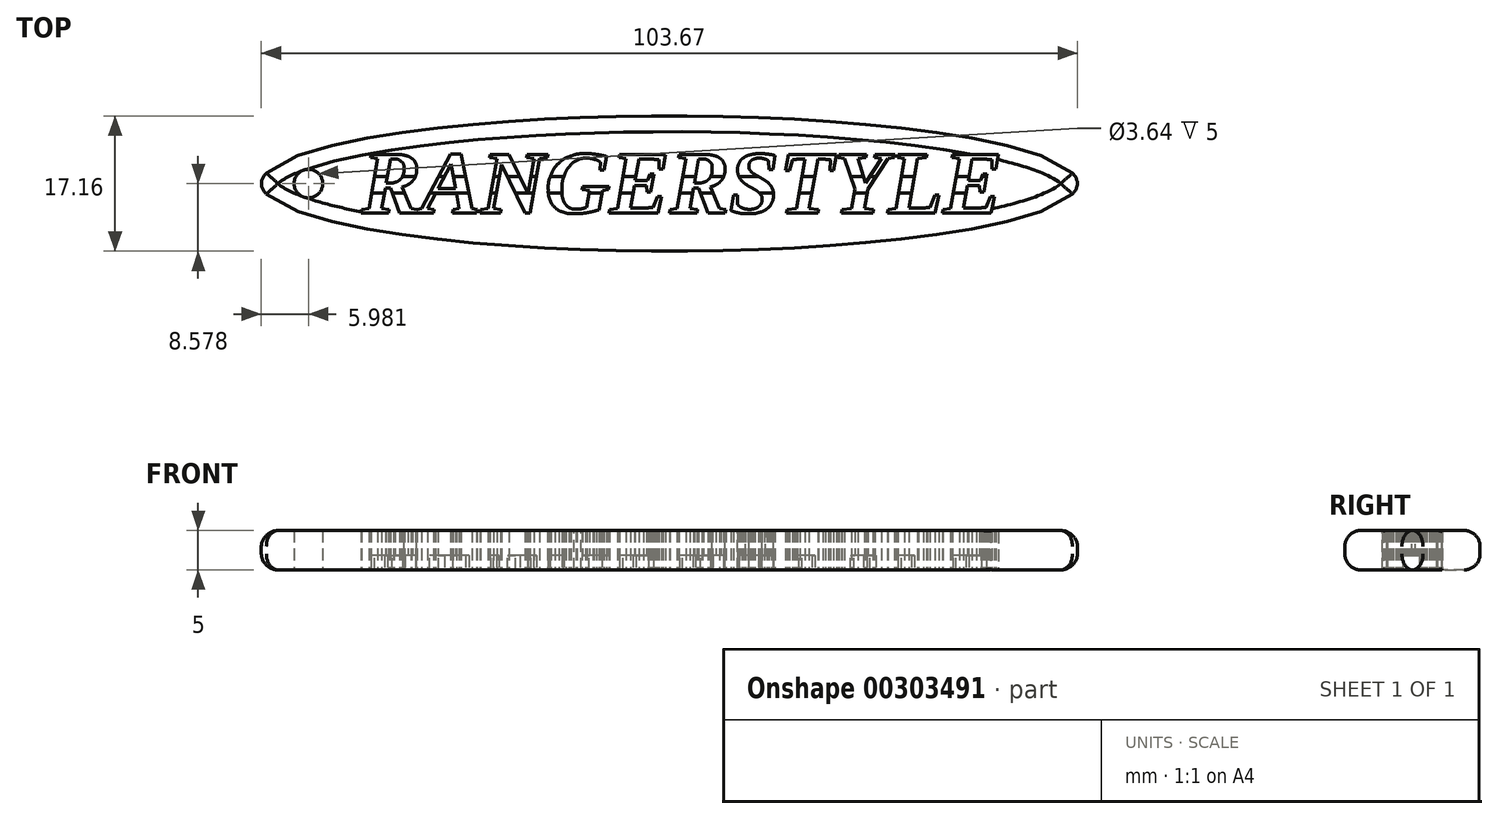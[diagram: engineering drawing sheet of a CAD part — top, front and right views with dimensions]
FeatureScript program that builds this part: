
annotation { "Feature Type Name" : "Feature", "Feature Type Description" : "" }
export const myFeature = defineFeature(function(context is Context, id is Id, definition is map)
    precondition{}
    {
        {
            var Q0;
            Q0=qCreatedBy(makeId("Top.planeOp"),FACE);
            var sketch = newSketch(context, id + "F0", { "sketchPlane" : qUnion([Q0])});
            skFitSpline(sketch, "E0", {"points": [v(-62.86, 19.24) * mm, v(-62.36, 19.24) * mm, v(-61.93, 19.2) * mm, v(-61.58, 19.12) * mm]});
            skFitSpline(sketch, "E1", {"points": [v(-61.58, 19.12) * mm, v(-61.22, 19.04) * mm, v(-60.92, 18.92) * mm, v(-60.7, 18.76) * mm]});
            skFitSpline(sketch, "E2", {"points": [v(-60.7, 18.76) * mm, v(-60.46, 18.6) * mm, v(-60.3, 18.42) * mm, v(-60.18, 18.18) * mm]});
            skFitSpline(sketch, "E3", {"points": [v(-60.18, 18.18) * mm, v(-60.07, 17.95) * mm, v(-60.01, 17.68) * mm, v(-60.01, 17.37) * mm]});
            skFitSpline(sketch, "E4", {"points": [v(-60.01, 17.37) * mm, v(-60.01, 17.05) * mm, v(-60.06, 16.76) * mm, v(-60.15, 16.5) * mm]});
            skFitSpline(sketch, "E5", {"points": [v(-60.15, 16.5) * mm, v(-60.24, 16.26) * mm, v(-60.37, 16.04) * mm, v(-60.53, 15.86) * mm]});
            skFitSpline(sketch, "E6", {"points": [v(-60.53, 15.86) * mm, v(-60.7, 15.68) * mm, v(-60.9, 15.53) * mm, v(-61.12, 15.4) * mm]});
            skFitSpline(sketch, "E7", {"points": [v(-61.12, 15.4) * mm, v(-61.34, 15.28) * mm, v(-61.58, 15.18) * mm, v(-61.84, 15.11) * mm]});
            skLineSegment(sketch, "E8", {"start": v(-63.99, 14.96) * mm, "end": v(-64.45, 12.36) * mm});
            skLineSegment(sketch, "E9", {"start": v(-64.45, 12.36) * mm, "end": v(-63.52, 12.21) * mm});
            skLineSegment(sketch, "E10", {"start": v(-63.52, 12.21) * mm, "end": v(-63.59, 11.8) * mm});
            skLineSegment(sketch, "E11", {"start": v(-63.59, 11.8) * mm, "end": v(-67.06, 11.8) * mm});
            skLineSegment(sketch, "E12", {"start": v(-67.06, 11.8) * mm, "end": v(-67, 12.21) * mm});
            skLineSegment(sketch, "E13", {"start": v(-67, 12.21) * mm, "end": v(-66.09, 12.36) * mm});
            skLineSegment(sketch, "E14", {"start": v(-66.09, 12.36) * mm, "end": v(-64.97, 18.7) * mm});
            skLineSegment(sketch, "E15", {"start": v(-64.97, 18.7) * mm, "end": v(-65.9, 18.84) * mm});
            skLineSegment(sketch, "E16", {"start": v(-65.9, 18.84) * mm, "end": v(-65.83, 19.24) * mm});
            skLineSegment(sketch, "E17", {"start": v(-65.83, 19.24) * mm, "end": v(-62.86, 19.24) * mm});
            skFitSpline(sketch, "E18", {"points": [v(-63.58, 15.57) * mm, v(-63.27, 15.57) * mm, v(-63, 15.6) * mm, v(-62.76, 15.68) * mm]});
            skFitSpline(sketch, "E19", {"points": [v(-62.76, 15.68) * mm, v(-62.52, 15.76) * mm, v(-62.32, 15.87) * mm, v(-62.15, 16.02) * mm]});
            skFitSpline(sketch, "E20", {"points": [v(-62.15, 16.02) * mm, v(-61.99, 16.16) * mm, v(-61.86, 16.34) * mm, v(-61.77, 16.55) * mm]});
            skFitSpline(sketch, "E21", {"points": [v(-61.77, 16.55) * mm, v(-61.68, 16.77) * mm, v(-61.64, 17) * mm, v(-61.64, 17.28) * mm]});
            skFitSpline(sketch, "E22", {"points": [v(-61.64, 17.28) * mm, v(-61.64, 17.76) * mm, v(-61.75, 18.1) * mm, v(-61.98, 18.32) * mm]});
            skFitSpline(sketch, "E23", {"points": [v(-61.98, 18.32) * mm, v(-62.2, 18.53) * mm, v(-62.52, 18.63) * mm, v(-62.96, 18.63) * mm]});
            skLineSegment(sketch, "E24", {"start": v(-61.84, 15.11) * mm, "end": v(-60.72, 12.36) * mm});
            skLineSegment(sketch, "E25", {"start": v(-60.72, 12.36) * mm, "end": v(-59.9, 12.21) * mm});
            skLineSegment(sketch, "E26", {"start": v(-59.9, 12.21) * mm, "end": v(-59.97, 11.8) * mm});
            skLineSegment(sketch, "E27", {"start": v(-60.05, 11.8) * mm, "end": v(-62.2, 11.8) * mm});
            skLineSegment(sketch, "E28", {"start": v(-62.2, 11.8) * mm, "end": v(-63.34, 14.96) * mm});
            skLineSegment(sketch, "E29", {"start": v(-63.34, 14.96) * mm, "end": v(-63.99, 14.96) * mm});
            skLineSegment(sketch, "E30", {"start": v(-62.96, 18.63) * mm, "end": v(-63.34, 18.63) * mm});
            skLineSegment(sketch, "E31", {"start": v(-63.34, 18.63) * mm, "end": v(-63.88, 15.57) * mm});
            skLineSegment(sketch, "E32", {"start": v(-63.88, 15.57) * mm, "end": v(-63.58, 15.57) * mm});
            skLineSegment(sketch, "E33", {"start": v(-57.8, 12.21) * mm, "end": v(-57.87, 11.8) * mm});
            skLineSegment(sketch, "E34", {"start": v(-57.87, 11.8) * mm, "end": v(-60.05, 11.8) * mm});
            skLineSegment(sketch, "E35", {"start": v(-60.05, 11.8) * mm, "end": v(-59.97, 12.21) * mm});
            skLineSegment(sketch, "E36", {"start": v(-59.97, 12.21) * mm, "end": v(-59.4, 12.36) * mm});
            skLineSegment(sketch, "E37", {"start": v(-59.4, 12.36) * mm, "end": v(-55.7, 19.3) * mm});
            skLineSegment(sketch, "E38", {"start": v(-55.7, 19.3) * mm, "end": v(-54.37, 19.3) * mm});
            skLineSegment(sketch, "E39", {"start": v(-54.37, 19.3) * mm, "end": v(-52.96, 12.36) * mm});
            skLineSegment(sketch, "E40", {"start": v(-52.96, 12.36) * mm, "end": v(-52.36, 12.21) * mm});
            skLineSegment(sketch, "E41", {"start": v(-52.36, 12.21) * mm, "end": v(-52.44, 11.8) * mm});
            skLineSegment(sketch, "E42", {"start": v(-52.44, 11.8) * mm, "end": v(-55.48, 11.8) * mm});
            skLineSegment(sketch, "E43", {"start": v(-55.48, 11.8) * mm, "end": v(-55.4, 12.21) * mm});
            skLineSegment(sketch, "E44", {"start": v(-55.4, 12.21) * mm, "end": v(-54.64, 12.36) * mm});
            skLineSegment(sketch, "E45", {"start": v(-54.64, 12.36) * mm, "end": v(-54.97, 14.29) * mm});
            skLineSegment(sketch, "E46", {"start": v(-54.97, 14.29) * mm, "end": v(-57.6, 14.29) * mm});
            skLineSegment(sketch, "E47", {"start": v(-57.6, 14.29) * mm, "end": v(-58.61, 12.36) * mm});
            skLineSegment(sketch, "E48", {"start": v(-58.61, 12.36) * mm, "end": v(-57.8, 12.21) * mm});
            skLineSegment(sketch, "E49", {"start": v(-55.65, 18) * mm, "end": v(-57.28, 14.9) * mm});
            skLineSegment(sketch, "E50", {"start": v(-57.28, 14.9) * mm, "end": v(-55.09, 14.9) * mm});
            skLineSegment(sketch, "E51", {"start": v(-55.09, 14.9) * mm, "end": v(-55.65, 18) * mm});
            skFitSpline(sketch, "E52", {"points": [v(-43.3, 14.7) * mm, v(-43.3, 15.45) * mm, v(-43.17, 16.1) * mm, v(-42.93, 16.68) * mm]});
            skFitSpline(sketch, "E53", {"points": [v(-42.93, 16.68) * mm, v(-42.69, 17.25) * mm, v(-42.35, 17.74) * mm, v(-41.93, 18.13) * mm]});
            skFitSpline(sketch, "E54", {"points": [v(-41.93, 18.13) * mm, v(-41.5, 18.52) * mm, v(-41, 18.82) * mm, v(-40.42, 19.02) * mm]});
            skFitSpline(sketch, "E55", {"points": [v(-40.42, 19.02) * mm, v(-39.85, 19.22) * mm, v(-39.23, 19.32) * mm, v(-38.56, 19.32) * mm]});
            skFitSpline(sketch, "E56", {"points": [v(-38.56, 19.32) * mm, v(-38.05, 19.32) * mm, v(-37.58, 19.3) * mm, v(-37.15, 19.23) * mm]});
            skFitSpline(sketch, "E57", {"points": [v(-37.15, 19.23) * mm, v(-36.73, 19.17) * mm, v(-36.32, 19.09) * mm, v(-35.92, 18.98) * mm]});
            skLineSegment(sketch, "E58", {"start": v(-45.1, 18.7) * mm, "end": v(-46.06, 18.84) * mm});
            skLineSegment(sketch, "E59", {"start": v(-46.06, 18.84) * mm, "end": v(-45.99, 19.24) * mm});
            skLineSegment(sketch, "E60", {"start": v(-45.99, 19.24) * mm, "end": v(-43.35, 19.24) * mm});
            skLineSegment(sketch, "E61", {"start": v(-43.35, 19.24) * mm, "end": v(-43.42, 18.84) * mm});
            skLineSegment(sketch, "E62", {"start": v(-43.42, 18.84) * mm, "end": v(-44.4, 18.7) * mm});
            skLineSegment(sketch, "E63", {"start": v(-44.4, 18.7) * mm, "end": v(-45.6, 11.8) * mm});
            skLineSegment(sketch, "E64", {"start": v(-45.6, 11.8) * mm, "end": v(-46.24, 11.8) * mm});
            skLineSegment(sketch, "E65", {"start": v(-46.24, 11.8) * mm, "end": v(-49.24, 17.97) * mm});
            skLineSegment(sketch, "E66", {"start": v(-49.24, 17.97) * mm, "end": v(-50.25, 12.36) * mm});
            skLineSegment(sketch, "E67", {"start": v(-50.25, 12.36) * mm, "end": v(-49.28, 12.21) * mm});
            skLineSegment(sketch, "E68", {"start": v(-49.28, 12.21) * mm, "end": v(-49.34, 11.8) * mm});
            skLineSegment(sketch, "E69", {"start": v(-49.34, 11.8) * mm, "end": v(-51.99, 11.8) * mm});
            skLineSegment(sketch, "E70", {"start": v(-51.99, 11.8) * mm, "end": v(-51.92, 12.21) * mm});
            skLineSegment(sketch, "E71", {"start": v(-51.92, 12.21) * mm, "end": v(-50.94, 12.36) * mm});
            skLineSegment(sketch, "E72", {"start": v(-50.94, 12.36) * mm, "end": v(-49.83, 18.7) * mm});
            skLineSegment(sketch, "E73", {"start": v(-49.83, 18.7) * mm, "end": v(-50.75, 18.84) * mm});
            skLineSegment(sketch, "E74", {"start": v(-50.75, 18.84) * mm, "end": v(-50.68, 19.24) * mm});
            skLineSegment(sketch, "E75", {"start": v(-50.68, 19.24) * mm, "end": v(-48.28, 19.24) * mm});
            skLineSegment(sketch, "E76", {"start": v(-48.28, 19.24) * mm, "end": v(-45.87, 14.29) * mm});
            skLineSegment(sketch, "E77", {"start": v(-45.87, 14.29) * mm, "end": v(-45.1, 18.7) * mm});
            skFitSpline(sketch, "E78", {"points": [v(-36.69, 18.24) * mm, v(-36.9, 18.4) * mm, v(-37.16, 18.52) * mm, v(-37.46, 18.6) * mm]});
            skFitSpline(sketch, "E79", {"points": [v(-37.46, 18.6) * mm, v(-37.75, 18.7) * mm, v(-38.09, 18.74) * mm, v(-38.46, 18.74) * mm]});
            skFitSpline(sketch, "E80", {"points": [v(-38.46, 18.74) * mm, v(-38.88, 18.74) * mm, v(-39.27, 18.65) * mm, v(-39.65, 18.47) * mm]});
            skFitSpline(sketch, "E81", {"points": [v(-39.65, 18.47) * mm, v(-40.02, 18.29) * mm, v(-40.35, 18.02) * mm, v(-40.64, 17.67) * mm]});
            skFitSpline(sketch, "E82", {"points": [v(-40.64, 17.67) * mm, v(-40.92, 17.33) * mm, v(-41.15, 16.9) * mm, v(-41.32, 16.38) * mm]});
            skFitSpline(sketch, "E83", {"points": [v(-41.32, 16.38) * mm, v(-41.48, 15.86) * mm, v(-41.57, 15.26) * mm, v(-41.57, 14.6) * mm]});
            skFitSpline(sketch, "E84", {"points": [v(-41.57, 14.6) * mm, v(-41.57, 14.2) * mm, v(-41.52, 13.87) * mm, v(-41.43, 13.58) * mm]});
            skFitSpline(sketch, "E85", {"points": [v(-41.43, 13.58) * mm, v(-41.34, 13.28) * mm, v(-41.22, 13.04) * mm, v(-41.06, 12.84) * mm]});
            skFitSpline(sketch, "E86", {"points": [v(-41.06, 12.84) * mm, v(-40.9, 12.65) * mm, v(-40.71, 12.5) * mm, v(-40.5, 12.41) * mm]});
            skFitSpline(sketch, "E87", {"points": [v(-40.5, 12.41) * mm, v(-40.27, 12.32) * mm, v(-40.02, 12.27) * mm, v(-39.75, 12.27) * mm]});
            skFitSpline(sketch, "E88", {"points": [v(-39.75, 12.27) * mm, v(-39.47, 12.27) * mm, v(-39.21, 12.3) * mm, v(-38.98, 12.35) * mm]});
            skFitSpline(sketch, "E89", {"points": [v(-38.98, 12.35) * mm, v(-38.75, 12.4) * mm, v(-38.57, 12.45) * mm, v(-38.44, 12.5) * mm]});
            skLineSegment(sketch, "E90", {"start": v(-35.92, 18.98) * mm, "end": v(-36.23, 17.27) * mm});
            skLineSegment(sketch, "E91", {"start": v(-36.23, 17.27) * mm, "end": v(-36.7, 17.27) * mm});
            skLineSegment(sketch, "E92", {"start": v(-36.7, 17.27) * mm, "end": v(-36.69, 18.24) * mm});
            skFitSpline(sketch, "E93", {"points": [v(-36.85, 12.2) * mm, v(-37.1, 12.12) * mm, v(-37.35, 12.05) * mm, v(-37.6, 11.99) * mm]});
            skFitSpline(sketch, "E94", {"points": [v(-37.6, 11.99) * mm, v(-37.84, 11.93) * mm, v(-38.09, 11.87) * mm, v(-38.35, 11.83) * mm]});
            skFitSpline(sketch, "E95", {"points": [v(-38.35, 11.83) * mm, v(-38.6, 11.79) * mm, v(-38.87, 11.75) * mm, v(-39.14, 11.73) * mm]});
            skFitSpline(sketch, "E96", {"points": [v(-39.14, 11.73) * mm, v(-39.42, 11.7) * mm, v(-39.7, 11.7) * mm, v(-40, 11.7) * mm]});
            skFitSpline(sketch, "E97", {"points": [v(-40, 11.7) * mm, v(-40.53, 11.7) * mm, v(-41, 11.77) * mm, v(-41.41, 11.9) * mm]});
            skFitSpline(sketch, "E98", {"points": [v(-41.41, 11.9) * mm, v(-41.82, 12.04) * mm, v(-42.16, 12.24) * mm, v(-42.44, 12.5) * mm]});
            skFitSpline(sketch, "E99", {"points": [v(-42.44, 12.5) * mm, v(-42.72, 12.76) * mm, v(-42.93, 13.08) * mm, v(-43.07, 13.45) * mm]});
            skFitSpline(sketch, "E100", {"points": [v(-43.07, 13.45) * mm, v(-43.22, 13.82) * mm, v(-43.3, 14.24) * mm, v(-43.3, 14.7) * mm]});
            skLineSegment(sketch, "E101", {"start": v(-38.44, 12.5) * mm, "end": v(-38.06, 14.61) * mm});
            skLineSegment(sketch, "E102", {"start": v(-38.06, 14.61) * mm, "end": v(-38.99, 14.8) * mm});
            skLineSegment(sketch, "E103", {"start": v(-38.99, 14.8) * mm, "end": v(-38.92, 15.17) * mm});
            skLineSegment(sketch, "E104", {"start": v(-38.92, 15.17) * mm, "end": v(-35.6, 15.17) * mm});
            skLineSegment(sketch, "E105", {"start": v(-35.6, 15.17) * mm, "end": v(-35.67, 14.8) * mm});
            skLineSegment(sketch, "E106", {"start": v(-35.67, 14.8) * mm, "end": v(-36.43, 14.61) * mm});
            skLineSegment(sketch, "E107", {"start": v(-36.43, 14.61) * mm, "end": v(-36.85, 12.2) * mm});
            skFitSpline(sketch, "E108", {"points": [v(-29.22, 18.55) * mm, v(-29.34, 18.57) * mm, v(-29.47, 18.58) * mm, v(-29.63, 18.6) * mm]});
            skFitSpline(sketch, "E109", {"points": [v(-29.63, 18.6) * mm, v(-29.78, 18.6) * mm, v(-29.94, 18.61) * mm, v(-30.1, 18.61) * mm]});
            skFitSpline(sketch, "E110", {"points": [v(-30.1, 18.61) * mm, v(-30.27, 18.62) * mm, v(-30.43, 18.63) * mm, v(-30.59, 18.63) * mm]});
            skFitSpline(sketch, "E111", {"points": [v(-30.59, 18.63) * mm, v(-30.74, 18.63) * mm, v(-30.88, 18.63) * mm, v(-31, 18.63) * mm]});
            skLineSegment(sketch, "E112", {"start": v(-35.5, 12.21) * mm, "end": v(-34.51, 12.36) * mm});
            skLineSegment(sketch, "E113", {"start": v(-34.51, 12.36) * mm, "end": v(-33.4, 18.7) * mm});
            skLineSegment(sketch, "E114", {"start": v(-33.4, 18.7) * mm, "end": v(-34.32, 18.84) * mm});
            skLineSegment(sketch, "E115", {"start": v(-34.32, 18.84) * mm, "end": v(-34.25, 19.24) * mm});
            skLineSegment(sketch, "E116", {"start": v(-34.25, 19.24) * mm, "end": v(-28.42, 19.24) * mm});
            skLineSegment(sketch, "E117", {"start": v(-28.42, 19.24) * mm, "end": v(-28.75, 17.35) * mm});
            skLineSegment(sketch, "E118", {"start": v(-28.75, 17.35) * mm, "end": v(-29.26, 17.35) * mm});
            skLineSegment(sketch, "E119", {"start": v(-29.26, 17.35) * mm, "end": v(-29.22, 18.55) * mm});
            skFitSpline(sketch, "E120", {"points": [v(-31.85, 12.42) * mm, v(-31.62, 12.42) * mm, v(-31.4, 12.42) * mm, v(-31.2, 12.42) * mm]});
            skFitSpline(sketch, "E121", {"points": [v(-31.2, 12.42) * mm, v(-31, 12.43) * mm, v(-30.82, 12.44) * mm, v(-30.66, 12.45) * mm]});
            skFitSpline(sketch, "E122", {"points": [v(-30.66, 12.45) * mm, v(-30.5, 12.45) * mm, v(-30.36, 12.46) * mm, v(-30.24, 12.47) * mm]});
            skFitSpline(sketch, "E123", {"points": [v(-30.24, 12.47) * mm, v(-30.12, 12.48) * mm, v(-30.04, 12.5) * mm, v(-29.98, 12.5) * mm]});
            skLineSegment(sketch, "E124", {"start": v(-31, 18.63) * mm, "end": v(-31.77, 18.63) * mm});
            skLineSegment(sketch, "E125", {"start": v(-31.77, 18.63) * mm, "end": v(-32.25, 15.9) * mm});
            skLineSegment(sketch, "E126", {"start": v(-32.25, 15.9) * mm, "end": v(-30.7, 15.9) * mm});
            skLineSegment(sketch, "E127", {"start": v(-30.7, 15.9) * mm, "end": v(-30.38, 16.72) * mm});
            skLineSegment(sketch, "E128", {"start": v(-30.38, 16.72) * mm, "end": v(-29.88, 16.72) * mm});
            skLineSegment(sketch, "E129", {"start": v(-29.88, 16.72) * mm, "end": v(-30.29, 14.44) * mm});
            skLineSegment(sketch, "E130", {"start": v(-30.29, 14.44) * mm, "end": v(-30.78, 14.44) * mm});
            skLineSegment(sketch, "E131", {"start": v(-30.78, 14.44) * mm, "end": v(-30.8, 15.28) * mm});
            skLineSegment(sketch, "E132", {"start": v(-30.8, 15.28) * mm, "end": v(-32.36, 15.28) * mm});
            skLineSegment(sketch, "E133", {"start": v(-32.36, 15.28) * mm, "end": v(-32.86, 12.42) * mm});
            skLineSegment(sketch, "E134", {"start": v(-32.86, 12.42) * mm, "end": v(-31.85, 12.42) * mm});
            skLineSegment(sketch, "E135", {"start": v(-29.98, 12.5) * mm, "end": v(-29.4, 13.88) * mm});
            skLineSegment(sketch, "E136", {"start": v(-29.4, 13.88) * mm, "end": v(-28.9, 13.88) * mm});
            skLineSegment(sketch, "E137", {"start": v(-28.9, 13.88) * mm, "end": v(-29.37, 11.8) * mm});
            skLineSegment(sketch, "E138", {"start": v(-29.37, 11.8) * mm, "end": v(-35.56, 11.8) * mm});
            skLineSegment(sketch, "E139", {"start": v(-35.56, 11.8) * mm, "end": v(-35.5, 12.21) * mm});
            skLineSegment(sketch, "E140", {"start": v(-35.5, 12.21) * mm, "end": v(-35.5, 12.21) * mm});
            skLineSegment(sketch, "E141", {"start": v(-31.63, 12.42) * mm, "end": v(-29.98, 12.5) * mm});
            skFitSpline(sketch, "E142", {"points": [v(-23.7, 19.24) * mm, v(-23.2, 19.24) * mm, v(-22.78, 19.2) * mm, v(-22.42, 19.12) * mm]});
            skFitSpline(sketch, "E143", {"points": [v(-22.42, 19.12) * mm, v(-22.06, 19.04) * mm, v(-21.77, 18.92) * mm, v(-21.54, 18.76) * mm]});
            skFitSpline(sketch, "E144", {"points": [v(-21.54, 18.76) * mm, v(-21.3, 18.6) * mm, v(-21.14, 18.42) * mm, v(-21.02, 18.18) * mm]});
            skFitSpline(sketch, "E145", {"points": [v(-21.02, 18.18) * mm, v(-20.91, 17.95) * mm, v(-20.86, 17.68) * mm, v(-20.86, 17.37) * mm]});
            skFitSpline(sketch, "E146", {"points": [v(-20.86, 17.37) * mm, v(-20.86, 17.05) * mm, v(-20.9, 16.76) * mm, v(-21, 16.5) * mm]});
            skFitSpline(sketch, "E147", {"points": [v(-21, 16.5) * mm, v(-21.09, 16.26) * mm, v(-21.22, 16.04) * mm, v(-21.38, 15.86) * mm]});
            skFitSpline(sketch, "E148", {"points": [v(-21.38, 15.86) * mm, v(-21.54, 15.68) * mm, v(-21.74, 15.53) * mm, v(-21.96, 15.4) * mm]});
            skFitSpline(sketch, "E149", {"points": [v(-21.96, 15.4) * mm, v(-22.18, 15.28) * mm, v(-22.42, 15.18) * mm, v(-22.68, 15.11) * mm]});
            skLineSegment(sketch, "E150", {"start": v(-24.83, 14.96) * mm, "end": v(-25.3, 12.36) * mm});
            skLineSegment(sketch, "E151", {"start": v(-25.3, 12.36) * mm, "end": v(-24.37, 12.21) * mm});
            skLineSegment(sketch, "E152", {"start": v(-24.37, 12.21) * mm, "end": v(-24.43, 11.8) * mm});
            skLineSegment(sketch, "E153", {"start": v(-24.43, 11.8) * mm, "end": v(-27.9, 11.8) * mm});
            skLineSegment(sketch, "E154", {"start": v(-27.9, 11.8) * mm, "end": v(-27.84, 12.21) * mm});
            skLineSegment(sketch, "E155", {"start": v(-27.84, 12.21) * mm, "end": v(-26.93, 12.36) * mm});
            skLineSegment(sketch, "E156", {"start": v(-26.93, 12.36) * mm, "end": v(-25.82, 18.7) * mm});
            skLineSegment(sketch, "E157", {"start": v(-25.82, 18.7) * mm, "end": v(-26.74, 18.84) * mm});
            skLineSegment(sketch, "E158", {"start": v(-26.74, 18.84) * mm, "end": v(-26.67, 19.24) * mm});
            skLineSegment(sketch, "E159", {"start": v(-26.67, 19.24) * mm, "end": v(-23.7, 19.24) * mm});
            skFitSpline(sketch, "E160", {"points": [v(-24.42, 15.57) * mm, v(-24.12, 15.57) * mm, v(-23.85, 15.6) * mm, v(-23.6, 15.68) * mm]});
            skFitSpline(sketch, "E161", {"points": [v(-23.6, 15.68) * mm, v(-23.37, 15.76) * mm, v(-23.16, 15.87) * mm, v(-23, 16.02) * mm]});
            skFitSpline(sketch, "E162", {"points": [v(-23, 16.02) * mm, v(-22.83, 16.16) * mm, v(-22.7, 16.34) * mm, v(-22.62, 16.55) * mm]});
            skFitSpline(sketch, "E163", {"points": [v(-22.62, 16.55) * mm, v(-22.53, 16.77) * mm, v(-22.48, 17) * mm, v(-22.48, 17.28) * mm]});
            skFitSpline(sketch, "E164", {"points": [v(-22.48, 17.28) * mm, v(-22.48, 17.76) * mm, v(-22.6, 18.1) * mm, v(-22.82, 18.32) * mm]});
            skFitSpline(sketch, "E165", {"points": [v(-22.82, 18.32) * mm, v(-23.04, 18.53) * mm, v(-23.37, 18.63) * mm, v(-23.8, 18.63) * mm]});
            skLineSegment(sketch, "E166", {"start": v(-22.68, 15.11) * mm, "end": v(-21.57, 12.36) * mm});
            skLineSegment(sketch, "E167", {"start": v(-21.57, 12.36) * mm, "end": v(-20.75, 12.21) * mm});
            skLineSegment(sketch, "E168", {"start": v(-20.75, 12.21) * mm, "end": v(-20.82, 11.8) * mm});
            skLineSegment(sketch, "E169", {"start": v(-20.82, 11.8) * mm, "end": v(-23.04, 11.8) * mm});
            skLineSegment(sketch, "E170", {"start": v(-23.04, 11.8) * mm, "end": v(-24.19, 14.96) * mm});
            skLineSegment(sketch, "E171", {"start": v(-24.19, 14.96) * mm, "end": v(-24.83, 14.96) * mm});
            skFitSpline(sketch, "E172", {"points": [v(-17.92, 11.7) * mm, v(-18.4, 11.7) * mm, v(-18.83, 11.74) * mm, v(-19.2, 11.82) * mm]});
            skFitSpline(sketch, "E173", {"points": [v(-19.2, 11.82) * mm, v(-19.56, 11.9) * mm, v(-19.86, 12) * mm, v(-20.1, 12.1) * mm]});
            skLineSegment(sketch, "E174", {"start": v(-23.8, 18.63) * mm, "end": v(-24.18, 18.63) * mm});
            skLineSegment(sketch, "E175", {"start": v(-24.18, 18.63) * mm, "end": v(-24.73, 15.57) * mm});
            skLineSegment(sketch, "E176", {"start": v(-24.73, 15.57) * mm, "end": v(-24.42, 15.57) * mm});
            skFitSpline(sketch, "E177", {"points": [v(-19.26, 12.9) * mm, v(-19.2, 12.8) * mm, v(-19.11, 12.72) * mm, v(-19.01, 12.64) * mm]});
            skFitSpline(sketch, "E178", {"points": [v(-19.01, 12.64) * mm, v(-18.9, 12.56) * mm, v(-18.8, 12.5) * mm, v(-18.67, 12.43) * mm]});
            skFitSpline(sketch, "E179", {"points": [v(-18.67, 12.43) * mm, v(-18.54, 12.38) * mm, v(-18.4, 12.33) * mm, v(-18.26, 12.3) * mm]});
            skFitSpline(sketch, "E180", {"points": [v(-18.26, 12.3) * mm, v(-18.12, 12.27) * mm, v(-17.97, 12.26) * mm, v(-17.82, 12.26) * mm]});
            skFitSpline(sketch, "E181", {"points": [v(-17.82, 12.26) * mm, v(-17.53, 12.26) * mm, v(-17.28, 12.29) * mm, v(-17.07, 12.35) * mm]});
            skFitSpline(sketch, "E182", {"points": [v(-17.07, 12.35) * mm, v(-16.85, 12.42) * mm, v(-16.68, 12.5) * mm, v(-16.54, 12.62) * mm]});
            skFitSpline(sketch, "E183", {"points": [v(-16.54, 12.62) * mm, v(-16.4, 12.74) * mm, v(-16.3, 12.87) * mm, v(-16.24, 13.03) * mm]});
            skFitSpline(sketch, "E184", {"points": [v(-16.24, 13.03) * mm, v(-16.17, 13.18) * mm, v(-16.14, 13.35) * mm, v(-16.14, 13.53) * mm]});
            skFitSpline(sketch, "E185", {"points": [v(-16.14, 13.53) * mm, v(-16.14, 13.73) * mm, v(-16.18, 13.9) * mm, v(-16.27, 14.05) * mm]});
            skFitSpline(sketch, "E186", {"points": [v(-16.27, 14.05) * mm, v(-16.36, 14.2) * mm, v(-16.48, 14.33) * mm, v(-16.62, 14.45) * mm]});
            skFitSpline(sketch, "E187", {"points": [v(-16.62, 14.45) * mm, v(-16.77, 14.57) * mm, v(-16.93, 14.69) * mm, v(-17.12, 14.8) * mm]});
            skFitSpline(sketch, "E188", {"points": [v(-17.12, 14.8) * mm, v(-17.3, 14.9) * mm, v(-17.5, 15) * mm, v(-17.69, 15.11) * mm]});
            skFitSpline(sketch, "E189", {"points": [v(-17.69, 15.11) * mm, v(-17.88, 15.22) * mm, v(-18.07, 15.34) * mm, v(-18.25, 15.47) * mm]});
            skFitSpline(sketch, "E190", {"points": [v(-18.25, 15.47) * mm, v(-18.44, 15.6) * mm, v(-18.6, 15.74) * mm, v(-18.75, 15.9) * mm]});
            skFitSpline(sketch, "E191", {"points": [v(-18.75, 15.9) * mm, v(-18.9, 16.08) * mm, v(-19.01, 16.27) * mm, v(-19.1, 16.48) * mm]});
            skFitSpline(sketch, "E192", {"points": [v(-19.1, 16.48) * mm, v(-19.19, 16.7) * mm, v(-19.23, 16.95) * mm, v(-19.23, 17.23) * mm]});
            skFitSpline(sketch, "E193", {"points": [v(-19.23, 17.23) * mm, v(-19.23, 17.59) * mm, v(-19.17, 17.9) * mm, v(-19.04, 18.15) * mm]});
            skFitSpline(sketch, "E194", {"points": [v(-19.04, 18.15) * mm, v(-18.9, 18.42) * mm, v(-18.72, 18.63) * mm, v(-18.47, 18.8) * mm]});
            skFitSpline(sketch, "E195", {"points": [v(-18.47, 18.8) * mm, v(-18.22, 18.98) * mm, v(-17.91, 19.11) * mm, v(-17.55, 19.2) * mm]});
            skFitSpline(sketch, "E196", {"points": [v(-17.55, 19.2) * mm, v(-17.2, 19.28) * mm, v(-16.79, 19.32) * mm, v(-16.34, 19.32) * mm]});
            skFitSpline(sketch, "E197", {"points": [v(-16.34, 19.32) * mm, v(-16.02, 19.32) * mm, v(-15.7, 19.3) * mm, v(-15.37, 19.26) * mm]});
            skFitSpline(sketch, "E198", {"points": [v(-15.37, 19.26) * mm, v(-15.04, 19.21) * mm, v(-14.74, 19.16) * mm, v(-14.47, 19.09) * mm]});
            skLineSegment(sketch, "E199", {"start": v(-20.1, 12.1) * mm, "end": v(-19.75, 14.09) * mm});
            skLineSegment(sketch, "E200", {"start": v(-19.75, 14.09) * mm, "end": v(-19.26, 14.09) * mm});
            skLineSegment(sketch, "E201", {"start": v(-19.26, 14.09) * mm, "end": v(-19.26, 12.9) * mm});
            skFitSpline(sketch, "E202", {"points": [v(-15.32, 18.4) * mm, v(-15.46, 18.51) * mm, v(-15.63, 18.6) * mm, v(-15.83, 18.65) * mm]});
            skFitSpline(sketch, "E203", {"points": [v(-15.83, 18.65) * mm, v(-16.02, 18.72) * mm, v(-16.24, 18.75) * mm, v(-16.49, 18.75) * mm]});
            skFitSpline(sketch, "E204", {"points": [v(-16.49, 18.75) * mm, v(-16.72, 18.75) * mm, v(-16.92, 18.72) * mm, v(-17.1, 18.66) * mm]});
            skFitSpline(sketch, "E205", {"points": [v(-17.1, 18.66) * mm, v(-17.26, 18.6) * mm, v(-17.4, 18.54) * mm, v(-17.51, 18.44) * mm]});
            skFitSpline(sketch, "E206", {"points": [v(-17.51, 18.44) * mm, v(-17.62, 18.35) * mm, v(-17.7, 18.24) * mm, v(-17.75, 18.12) * mm]});
            skFitSpline(sketch, "E207", {"points": [v(-17.75, 18.12) * mm, v(-17.8, 18) * mm, v(-17.83, 17.87) * mm, v(-17.83, 17.73) * mm]});
            skFitSpline(sketch, "E208", {"points": [v(-17.83, 17.73) * mm, v(-17.83, 17.56) * mm, v(-17.78, 17.4) * mm, v(-17.7, 17.26) * mm]});
            skFitSpline(sketch, "E209", {"points": [v(-17.7, 17.26) * mm, v(-17.6, 17.13) * mm, v(-17.49, 17) * mm, v(-17.34, 16.89) * mm]});
            skFitSpline(sketch, "E210", {"points": [v(-17.34, 16.89) * mm, v(-17.2, 16.77) * mm, v(-17.02, 16.66) * mm, v(-16.84, 16.56) * mm]});
            skFitSpline(sketch, "E211", {"points": [v(-16.84, 16.56) * mm, v(-16.65, 16.45) * mm, v(-16.46, 16.35) * mm, v(-16.27, 16.24) * mm]});
            skFitSpline(sketch, "E212", {"points": [v(-16.27, 16.24) * mm, v(-16.07, 16.13) * mm, v(-15.88, 16) * mm, v(-15.7, 15.88) * mm]});
            skFitSpline(sketch, "E213", {"points": [v(-15.7, 15.88) * mm, v(-15.5, 15.75) * mm, v(-15.34, 15.6) * mm, v(-15.2, 15.44) * mm]});
            skFitSpline(sketch, "E214", {"points": [v(-15.2, 15.44) * mm, v(-15.05, 15.28) * mm, v(-14.93, 15.09) * mm, v(-14.84, 14.88) * mm]});
            skFitSpline(sketch, "E215", {"points": [v(-14.84, 14.88) * mm, v(-14.75, 14.67) * mm, v(-14.7, 14.43) * mm, v(-14.7, 14.15) * mm]});
            skFitSpline(sketch, "E216", {"points": [v(-14.7, 14.15) * mm, v(-14.7, 13.75) * mm, v(-14.78, 13.39) * mm, v(-14.92, 13.08) * mm]});
            skFitSpline(sketch, "E217", {"points": [v(-14.92, 13.08) * mm, v(-15.06, 12.78) * mm, v(-15.27, 12.52) * mm, v(-15.54, 12.31) * mm]});
            skFitSpline(sketch, "E218", {"points": [v(-15.54, 12.31) * mm, v(-15.82, 12.1) * mm, v(-16.15, 11.96) * mm, v(-16.55, 11.85) * mm]});
            skFitSpline(sketch, "E219", {"points": [v(-16.55, 11.85) * mm, v(-16.95, 11.75) * mm, v(-17.4, 11.7) * mm, v(-17.92, 11.7) * mm]});
            skLineSegment(sketch, "E220", {"start": v(-14.47, 19.09) * mm, "end": v(-14.78, 17.32) * mm});
            skLineSegment(sketch, "E221", {"start": v(-14.78, 17.32) * mm, "end": v(-15.28, 17.32) * mm});
            skLineSegment(sketch, "E222", {"start": v(-15.28, 17.32) * mm, "end": v(-15.32, 18.4) * mm});
            skFitSpline(sketch, "E223", {"points": [v(-11.02, 18.65) * mm, v(-11.1, 18.65) * mm, v(-11.2, 18.65) * mm, v(-11.32, 18.64) * mm]});
            skFitSpline(sketch, "E224", {"points": [v(-11.32, 18.64) * mm, v(-11.43, 18.64) * mm, v(-11.55, 18.63) * mm, v(-11.67, 18.62) * mm]});
            skFitSpline(sketch, "E225", {"points": [v(-11.67, 18.62) * mm, v(-11.78, 18.6) * mm, v(-11.9, 18.6) * mm, v(-12, 18.58) * mm]});
            skFitSpline(sketch, "E226", {"points": [v(-12, 18.58) * mm, v(-12.1, 18.57) * mm, v(-12.2, 18.56) * mm, v(-12.27, 18.54) * mm]});
            skLineSegment(sketch, "E227", {"start": v(-13.07, 11.8) * mm, "end": v(-13, 12.21) * mm});
            skLineSegment(sketch, "E228", {"start": v(-13, 12.21) * mm, "end": v(-11.8, 12.36) * mm});
            skLineSegment(sketch, "E229", {"start": v(-11.8, 12.36) * mm, "end": v(-10.68, 18.65) * mm});
            skLineSegment(sketch, "E230", {"start": v(-10.68, 18.65) * mm, "end": v(-11.02, 18.65) * mm});
            skFitSpline(sketch, "E231", {"points": [v(-7.47, 18.54) * mm, v(-7.53, 18.56) * mm, v(-7.62, 18.57) * mm, v(-7.73, 18.58) * mm]});
            skFitSpline(sketch, "E232", {"points": [v(-7.73, 18.58) * mm, v(-7.83, 18.6) * mm, v(-7.94, 18.6) * mm, v(-8.06, 18.6) * mm]});
            skFitSpline(sketch, "E233", {"points": [v(-8.06, 18.6) * mm, v(-8.18, 18.62) * mm, v(-8.3, 18.63) * mm, v(-8.41, 18.63) * mm]});
            skFitSpline(sketch, "E234", {"points": [v(-8.41, 18.63) * mm, v(-8.53, 18.64) * mm, v(-8.63, 18.64) * mm, v(-8.71, 18.64) * mm]});
            skLineSegment(sketch, "E235", {"start": v(-12.27, 18.54) * mm, "end": v(-12.68, 17.16) * mm});
            skLineSegment(sketch, "E236", {"start": v(-12.68, 17.16) * mm, "end": v(-13.16, 17.16) * mm});
            skLineSegment(sketch, "E237", {"start": v(-13.16, 17.16) * mm, "end": v(-12.8, 19.24) * mm});
            skLineSegment(sketch, "E238", {"start": v(-12.8, 19.24) * mm, "end": v(-6.69, 19.24) * mm});
            skLineSegment(sketch, "E239", {"start": v(-6.69, 19.24) * mm, "end": v(-7.05, 17.16) * mm});
            skLineSegment(sketch, "E240", {"start": v(-7.05, 17.16) * mm, "end": v(-7.54, 17.16) * mm});
            skLineSegment(sketch, "E241", {"start": v(-7.54, 17.16) * mm, "end": v(-7.47, 18.54) * mm});
            skLineSegment(sketch, "E242", {"start": v(-8.71, 18.64) * mm, "end": v(-9.04, 18.64) * mm});
            skLineSegment(sketch, "E243", {"start": v(-9.04, 18.64) * mm, "end": v(-10.15, 12.36) * mm});
            skLineSegment(sketch, "E244", {"start": v(-10.15, 12.36) * mm, "end": v(-9, 12.21) * mm});
            skLineSegment(sketch, "E245", {"start": v(-9, 12.21) * mm, "end": v(-9.06, 11.8) * mm});
            skLineSegment(sketch, "E246", {"start": v(-9.06, 11.8) * mm, "end": v(-13.07, 11.8) * mm});
            skLineSegment(sketch, "E247", {"start": v(-2.72, 14.85) * mm, "end": v(-3.16, 12.36) * mm});
            skLineSegment(sketch, "E248", {"start": v(-3.16, 12.36) * mm, "end": v(-2, 12.21) * mm});
            skLineSegment(sketch, "E249", {"start": v(-2, 12.21) * mm, "end": v(-2.07, 11.8) * mm});
            skLineSegment(sketch, "E250", {"start": v(-2.07, 11.8) * mm, "end": v(-6.08, 11.8) * mm});
            skLineSegment(sketch, "E251", {"start": v(-6.08, 11.8) * mm, "end": v(-6, 12.21) * mm});
            skLineSegment(sketch, "E252", {"start": v(-6, 12.21) * mm, "end": v(-4.8, 12.36) * mm});
            skLineSegment(sketch, "E253", {"start": v(-4.8, 12.36) * mm, "end": v(-4.36, 14.81) * mm});
            skLineSegment(sketch, "E254", {"start": v(-4.36, 14.81) * mm, "end": v(-5.66, 18.7) * mm});
            skLineSegment(sketch, "E255", {"start": v(-5.66, 18.7) * mm, "end": v(-6.47, 18.84) * mm});
            skLineSegment(sketch, "E256", {"start": v(-6.47, 18.84) * mm, "end": v(-6.4, 19.24) * mm});
            skLineSegment(sketch, "E257", {"start": v(-6.4, 19.24) * mm, "end": v(-2.87, 19.24) * mm});
            skLineSegment(sketch, "E258", {"start": v(-2.87, 19.24) * mm, "end": v(-2.94, 18.84) * mm});
            skLineSegment(sketch, "E259", {"start": v(-2.94, 18.84) * mm, "end": v(-3.97, 18.7) * mm});
            skLineSegment(sketch, "E260", {"start": v(-3.97, 18.7) * mm, "end": v(-2.98, 15.61) * mm});
            skLineSegment(sketch, "E261", {"start": v(-2.98, 15.61) * mm, "end": v(-0.97, 18.7) * mm});
            skLineSegment(sketch, "E262", {"start": v(-0.97, 18.7) * mm, "end": v(-1.85, 18.84) * mm});
            skLineSegment(sketch, "E263", {"start": v(-1.85, 18.84) * mm, "end": v(-1.77, 19.24) * mm});
            skLineSegment(sketch, "E264", {"start": v(-1.77, 19.24) * mm, "end": v(0.75, 19.24) * mm});
            skLineSegment(sketch, "E265", {"start": v(0.75, 19.24) * mm, "end": v(0.68, 18.84) * mm});
            skLineSegment(sketch, "E266", {"start": v(0.68, 18.84) * mm, "end": v(-0.13, 18.7) * mm});
            skLineSegment(sketch, "E267", {"start": v(-0.13, 18.7) * mm, "end": v(-2.72, 14.85) * mm});
            skFitSpline(sketch, "E268", {"points": [v(3.12, 12.4) * mm, v(3.31, 12.4) * mm, v(3.52, 12.4) * mm, v(3.74, 12.4) * mm]});
            skFitSpline(sketch, "E269", {"points": [v(3.74, 12.4) * mm, v(3.96, 12.41) * mm, v(4.17, 12.42) * mm, v(4.36, 12.43) * mm]});
            skFitSpline(sketch, "E270", {"points": [v(4.36, 12.43) * mm, v(4.56, 12.45) * mm, v(4.73, 12.46) * mm, v(4.88, 12.47) * mm]});
            skFitSpline(sketch, "E271", {"points": [v(4.88, 12.47) * mm, v(5.03, 12.48) * mm, v(5.14, 12.5) * mm, v(5.2, 12.5) * mm]});
            skLineSegment(sketch, "E272", {"start": v(4.72, 18.84) * mm, "end": v(3.6, 18.7) * mm});
            skLineSegment(sketch, "E273", {"start": v(3.6, 18.7) * mm, "end": v(2.5, 12.4) * mm});
            skLineSegment(sketch, "E274", {"start": v(2.5, 12.4) * mm, "end": v(3.12, 12.4) * mm});
            skLineSegment(sketch, "E275", {"start": v(5.2, 12.5) * mm, "end": v(5.85, 14.05) * mm});
            skLineSegment(sketch, "E276", {"start": v(5.85, 14.05) * mm, "end": v(6.31, 14.05) * mm});
            skLineSegment(sketch, "E277", {"start": v(6.31, 14.05) * mm, "end": v(5.82, 11.8) * mm});
            skLineSegment(sketch, "E278", {"start": v(5.82, 11.8) * mm, "end": v(-0.2, 11.8) * mm});
            skLineSegment(sketch, "E279", {"start": v(-0.2, 11.8) * mm, "end": v(-0.13, 12.21) * mm});
            skLineSegment(sketch, "E280", {"start": v(-0.13, 12.21) * mm, "end": v(0.85, 12.36) * mm});
            skLineSegment(sketch, "E281", {"start": v(0.85, 12.36) * mm, "end": v(1.97, 18.7) * mm});
            skLineSegment(sketch, "E282", {"start": v(1.97, 18.7) * mm, "end": v(1.05, 18.84) * mm});
            skLineSegment(sketch, "E283", {"start": v(1.05, 18.84) * mm, "end": v(1.12, 19.24) * mm});
            skLineSegment(sketch, "E284", {"start": v(1.12, 19.24) * mm, "end": v(4.8, 19.24) * mm});
            skLineSegment(sketch, "E285", {"start": v(4.8, 19.24) * mm, "end": v(4.72, 18.84) * mm});
            skFitSpline(sketch, "E286", {"points": [v(13.08, 18.55) * mm, v(12.97, 18.57) * mm, v(12.83, 18.58) * mm, v(12.68, 18.6) * mm]});
            skFitSpline(sketch, "E287", {"points": [v(12.68, 18.6) * mm, v(12.52, 18.6) * mm, v(12.37, 18.61) * mm, v(12.2, 18.61) * mm]});
            skFitSpline(sketch, "E288", {"points": [v(12.2, 18.61) * mm, v(12.04, 18.62) * mm, v(11.88, 18.63) * mm, v(11.72, 18.63) * mm]});
            skFitSpline(sketch, "E289", {"points": [v(11.72, 18.63) * mm, v(11.56, 18.63) * mm, v(11.42, 18.63) * mm, v(11.3, 18.63) * mm]});
            skLineSegment(sketch, "E290", {"start": v(6.81, 12.21) * mm, "end": v(7.8, 12.36) * mm});
            skLineSegment(sketch, "E291", {"start": v(7.8, 12.36) * mm, "end": v(8.9, 18.7) * mm});
            skLineSegment(sketch, "E292", {"start": v(8.9, 18.7) * mm, "end": v(7.98, 18.84) * mm});
            skLineSegment(sketch, "E293", {"start": v(7.98, 18.84) * mm, "end": v(8.05, 19.24) * mm});
            skLineSegment(sketch, "E294", {"start": v(8.05, 19.24) * mm, "end": v(13.88, 19.24) * mm});
            skLineSegment(sketch, "E295", {"start": v(13.88, 19.24) * mm, "end": v(13.55, 17.35) * mm});
            skLineSegment(sketch, "E296", {"start": v(13.55, 17.35) * mm, "end": v(13.05, 17.35) * mm});
            skLineSegment(sketch, "E297", {"start": v(13.05, 17.35) * mm, "end": v(13.08, 18.55) * mm});
            skFitSpline(sketch, "E298", {"points": [v(10.45, 12.42) * mm, v(10.68, 12.42) * mm, v(10.9, 12.42) * mm, v(11.1, 12.42) * mm]});
            skFitSpline(sketch, "E299", {"points": [v(11.1, 12.42) * mm, v(11.3, 12.43) * mm, v(11.48, 12.44) * mm, v(11.64, 12.45) * mm]});
            skFitSpline(sketch, "E300", {"points": [v(11.64, 12.45) * mm, v(11.8, 12.45) * mm, v(11.95, 12.46) * mm, v(12.06, 12.47) * mm]});
            skFitSpline(sketch, "E301", {"points": [v(12.06, 12.47) * mm, v(12.18, 12.48) * mm, v(12.27, 12.5) * mm, v(12.33, 12.5) * mm]});
            skLineSegment(sketch, "E302", {"start": v(11.3, 18.63) * mm, "end": v(10.54, 18.63) * mm});
            skLineSegment(sketch, "E303", {"start": v(10.54, 18.63) * mm, "end": v(10.05, 15.9) * mm});
            skLineSegment(sketch, "E304", {"start": v(10.05, 15.9) * mm, "end": v(11.61, 15.9) * mm});
            skLineSegment(sketch, "E305", {"start": v(11.61, 15.9) * mm, "end": v(11.93, 16.72) * mm});
            skLineSegment(sketch, "E306", {"start": v(11.93, 16.72) * mm, "end": v(12.42, 16.72) * mm});
            skLineSegment(sketch, "E307", {"start": v(12.42, 16.72) * mm, "end": v(12.02, 14.44) * mm});
            skLineSegment(sketch, "E308", {"start": v(12.02, 14.44) * mm, "end": v(11.52, 14.44) * mm});
            skLineSegment(sketch, "E309", {"start": v(11.52, 14.44) * mm, "end": v(11.5, 15.28) * mm});
            skLineSegment(sketch, "E310", {"start": v(11.5, 15.28) * mm, "end": v(9.94, 15.28) * mm});
            skLineSegment(sketch, "E311", {"start": v(9.94, 15.28) * mm, "end": v(9.44, 12.42) * mm});
            skLineSegment(sketch, "E312", {"start": v(9.44, 12.42) * mm, "end": v(10.45, 12.42) * mm});
            skLineSegment(sketch, "E313", {"start": v(12.33, 12.5) * mm, "end": v(12.9, 13.88) * mm});
            skLineSegment(sketch, "E314", {"start": v(12.9, 13.88) * mm, "end": v(13.4, 13.88) * mm});
            skLineSegment(sketch, "E315", {"start": v(13.4, 13.88) * mm, "end": v(12.94, 11.8) * mm});
            skLineSegment(sketch, "E316", {"start": v(12.94, 11.8) * mm, "end": v(6.75, 11.8) * mm});
            skLineSegment(sketch, "E317", {"start": v(6.75, 11.8) * mm, "end": v(6.81, 12.21) * mm});
            skLineSegment(sketch, "E318", {"start": v(6.81, 12.21) * mm, "end": v(6.81, 12.21) * mm});
            skLineSegment(sketch, "E319", {"start": v(10.67, 12.42) * mm, "end": v(12.33, 12.5) * mm});
            skSolve(sketch);
        }
        {
            var Q0;
            Q0=qCreatedBy(makeId("Top.planeOp"),FACE);
            var sketch = newSketch(context, id + "F1", { "sketchPlane" : qUnion([Q0])});
            skEllipse(sketch, "E320", {"center": v(-27.91, 15.53) * mm, "majorRadius": 51.83 * mm, "minorRadius": 8.58 * mm, "majorAxis": v(1, 0)});
            skCircle(sketch, "E321", {"center": v(-73.77, 15.53) * mm, "radius": 1.82 * mm});
            skPoint(sketch, "E321.centerSnap0", {"position": v(-79.75, 15.53) * mm});
            skSolve(sketch);
        }
        {
            var Q0;
            Q0=makeQuery(id+"F1.imprint","IMPRINT",FACE,{"disambiguationData":[TD([[makeQuery(id+"F1.imprint","IMPRINT",EDGE,{"derivedFrom":sQuery(id+"F1.wireOp",EDGE,"E320")}),1.0]])]});
            extrude(context, id + "F2", {"entities" : qUnion([Q0]), "depth" : 5 * mm});
        }
        {
            var Q0;
            Q0 = qSketchRegion(id + "F0", true);
            extrude(context, id + "F3", {"entities" : qUnion([Q0]), "operationType" : NewBodyOperationType.REMOVE, "depth" : 25 * mm});
        }
        {
            var Q0;
            Q0=qCreatedBy(makeId("Right.planeOp"),FACE);
            var sketch = newSketch(context, id + "F4", { "sketchPlane" : qUnion([Q0])});
            skLineSegment(sketch, "E322.bottom", {"start": v(16.43, 0) * mm, "end": v(14.33, 0) * mm});
            skLineSegment(sketch, "E322.top", {"start": v(16.43, 1.82) * mm, "end": v(14.33, 1.82) * mm});
            skLineSegment(sketch, "E322.left", {"start": v(16.43, 0) * mm, "end": v(16.43, 1.82) * mm});
            skLineSegment(sketch, "E322.right", {"start": v(14.33, 0) * mm, "end": v(14.33, 1.82) * mm});
            skSolve(sketch);
        }
        {
            var Q0;
            Q0 = qSketchRegion(id + "F4", true);
            extrude(context, id + "F5", {"entities" : qUnion([Q0]), "operationType" : NewBodyOperationType.ADD, "depth" : 20 * mm, "hasSecondDirection" : true, "secondDirectionOppositeDirection" : true, "secondDirectionDepth" : 70 * mm});
        }
        {
            var Q0;
            Q0=makeQuery(id+"F2.opExtrude","CAP_EDGE",EDGE,{"disambiguationData":[OSD([sQuery(id+"F1.wireOp",EDGE,"E320")])],"isStart":false});
            var Q1;
            Q1=makeQuery(id+"F2.opExtrude","CAP_EDGE",EDGE,{"disambiguationData":[OSD([sQuery(id+"F1.wireOp",EDGE,"E320")])],"isStart":true});
            fillet(context, id + "F6", {"entities" : qUnion([Q0, Q1]), "radius" : 2 * mm, "tangentPropagation" : true, "allowEdgeOverflow" : false});
        }
    });
